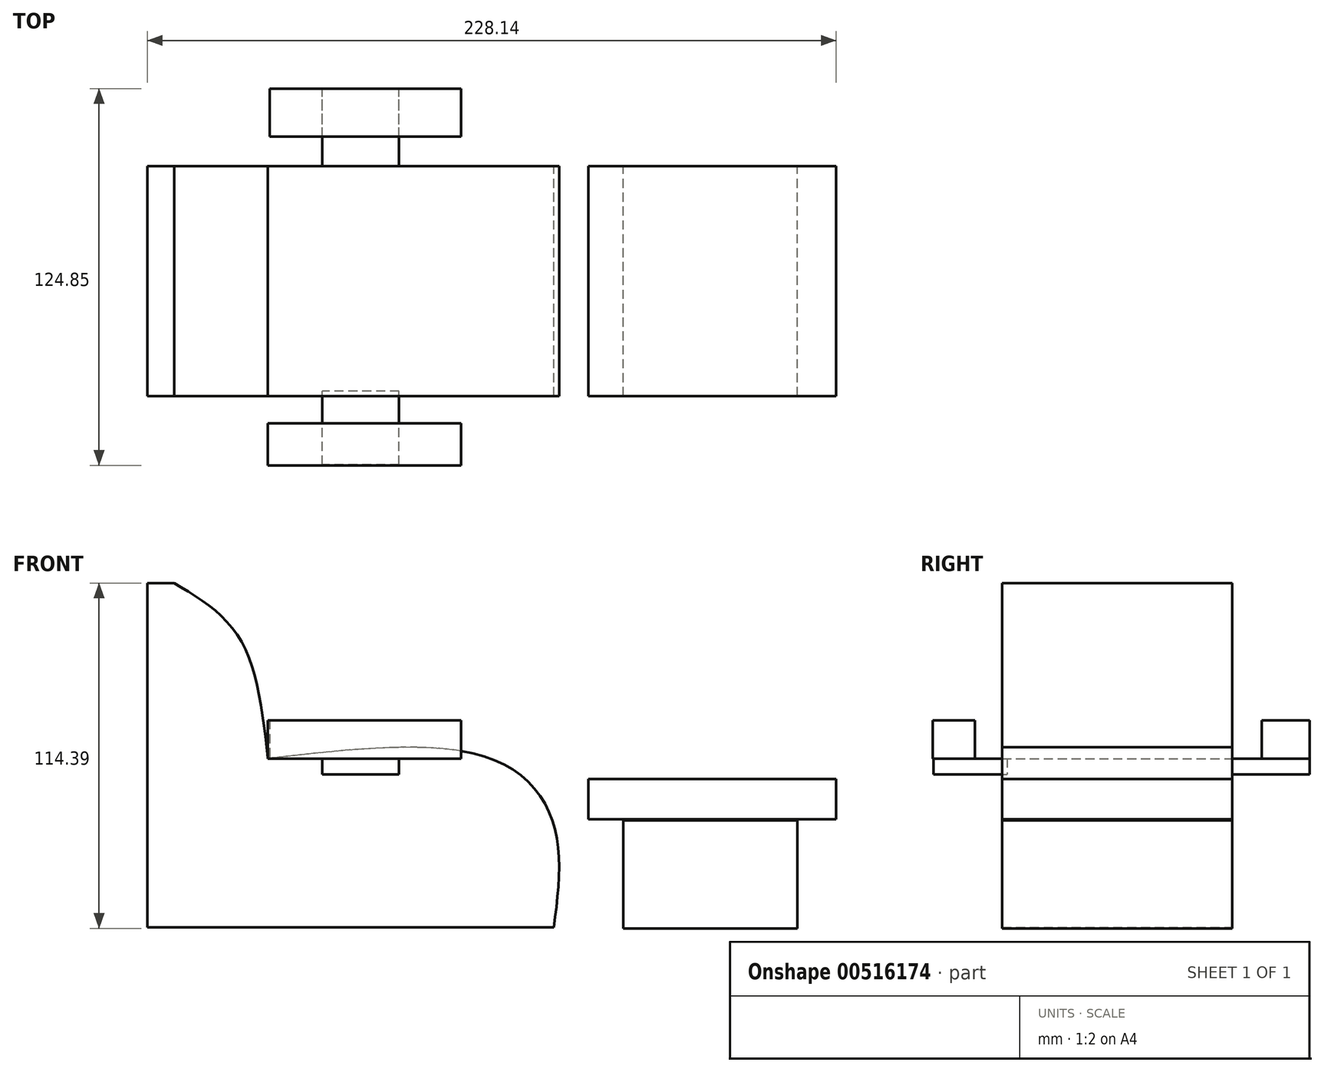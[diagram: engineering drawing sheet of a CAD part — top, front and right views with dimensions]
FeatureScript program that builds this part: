
annotation { "Feature Type Name" : "Feature", "Feature Type Description" : "" }
export const myFeature = defineFeature(function(context is Context, id is Id, definition is map)
    precondition{}
    {
        {
            var Q0;
            Q0=qCreatedBy(makeId("Front.planeOp"),FACE);
            var sketch = newSketch(context, id + "F0", { "sketchPlane" : qUnion([Q0])});
            skFitSpline(sketch, "E0", {"points": [v(-49.12, 58.15) * mm, v(-27.57, 40.08) * mm, v(-18.06, 0) * mm], "startDerivative": vector(54.48, -32.4) * mm, "endDerivative": vector(9.07, -82.3) * mm});
            skLineSegment(sketch, "E1", {"start": v(-49.12, 58.15) * mm, "end": v(-57.99, 58.15) * mm});
            skLineSegment(sketch, "E2", {"start": v(-57.99, 58.15) * mm, "end": v(-57.99, 0) * mm});
            skLineSegment(sketch, "E3", {"start": v(-57.99, 0) * mm, "end": v(-57.99, -55.93) * mm});
            skLineSegment(sketch, "E4", {"start": v(-57.99, -55.93) * mm, "end": v(76.68, -55.93) * mm});
            skFitSpline(sketch, "E5", {"points": [v(76.68, -55.93) * mm, v(76.68, -22.02) * mm, v(55.77, 0) * mm, v(-18.06, 0) * mm], "startDerivative": vector(15.36, 121.65) * mm, "endDerivative": vector(-195.91, -22.64) * mm});
            skSolve(sketch);
        }
        {
            var Q0;
            Q0 = qSketchRegion(id + "F0", true);
            extrude(context, id + "F1", {"entities" : qUnion([Q0]), "depth" : 76.2 * mm, "offsetDistance" : 25.4 * mm});
        }
        {
            var Q0;
            Q0=qCreatedBy(makeId("Top.planeOp"),FACE);
            var sketch = newSketch(context, id + "F2", { "sketchPlane" : qUnion([Q0])});
            skLineSegment(sketch, "E6.bottom", {"start": v(-18.09, -99.18) * mm, "end": v(45.92, -99.18) * mm});
            skLineSegment(sketch, "E6.top", {"start": v(-18.09, -85.24) * mm, "end": v(45.92, -85.24) * mm});
            skLineSegment(sketch, "E6.left", {"start": v(-18.09, -99.18) * mm, "end": v(-18.09, -85.24) * mm});
            skLineSegment(sketch, "E6.right", {"start": v(45.92, -99.18) * mm, "end": v(45.92, -85.24) * mm});
            skLineSegment(sketch, "E7.bottom", {"start": v(-17.45, 9.82) * mm, "end": v(45.92, 9.82) * mm});
            skLineSegment(sketch, "E7.top", {"start": v(-17.45, 25.67) * mm, "end": v(45.92, 25.67) * mm});
            skLineSegment(sketch, "E7.left", {"start": v(-17.45, 9.82) * mm, "end": v(-17.45, 25.67) * mm});
            skLineSegment(sketch, "E7.right", {"start": v(45.92, 9.82) * mm, "end": v(45.92, 25.67) * mm});
            skSolve(sketch);
        }
        {
            var Q0;
            Q0 = qSketchRegion(id + "F2", true);
            extrude(context, id + "F3", {"entities" : qUnion([Q0]), "depth" : 12.7 * mm, "offsetDistance" : 25.4 * mm});
        }
        {
            var Q0;
            Q0=qCreatedBy(makeId("Right.planeOp"),FACE);
            var sketch = newSketch(context, id + "F4", { "sketchPlane" : qUnion([Q0])});
            skLineSegment(sketch, "E8.bottom", {"start": v(0, 0) * mm, "end": v(25.58, 0) * mm});
            skLineSegment(sketch, "E8.top", {"start": v(0, -5.23) * mm, "end": v(25.58, -5.23) * mm});
            skLineSegment(sketch, "E8.left", {"start": v(0, 0) * mm, "end": v(0, -5.23) * mm});
            skLineSegment(sketch, "E8.right", {"start": v(25.58, 0) * mm, "end": v(25.58, -5.23) * mm});
            skLineSegment(sketch, "E9.bottom", {"start": v(-98.95, 0) * mm, "end": v(-74.55, 0) * mm});
            skLineSegment(sketch, "E9.top", {"start": v(-98.95, -5.23) * mm, "end": v(-74.55, -5.23) * mm});
            skLineSegment(sketch, "E9.left", {"start": v(-98.95, 0) * mm, "end": v(-98.95, -5.23) * mm});
            skLineSegment(sketch, "E9.right", {"start": v(-74.55, 0) * mm, "end": v(-74.55, -5.23) * mm});
            skSolve(sketch);
        }
        {
            var Q0;
            Q0 = qSketchRegion(id + "F4", true);
            extrude(context, id + "F5", {"entities" : qUnion([Q0]), "depth" : 25.4 * mm, "offsetDistance" : 25.4 * mm});
        }
        {
            var Q0;
            Q0=qCreatedBy(makeId("Front.planeOp"),FACE);
            var sketch = newSketch(context, id + "F6", { "sketchPlane" : qUnion([Q0])});
            skLineSegment(sketch, "E10.bottom", {"start": v(99.63, -20.44) * mm, "end": v(157.3, -20.44) * mm});
            skLineSegment(sketch, "E10.top", {"start": v(99.63, -56.24) * mm, "end": v(157.3, -56.24) * mm});
            skLineSegment(sketch, "E10.left", {"start": v(99.63, -20.44) * mm, "end": v(99.63, -56.24) * mm});
            skLineSegment(sketch, "E10.right", {"start": v(157.3, -20.44) * mm, "end": v(157.3, -56.24) * mm});
            skSolve(sketch);
        }
        {
            var Q0;
            Q0 = qSketchRegion(id + "F6", true);
            extrude(context, id + "F7", {"entities" : qUnion([Q0]), "depth" : 76.2 * mm, "offsetDistance" : 25.4 * mm});
        }
        {
            var Q0;
            Q0=qCreatedBy(makeId("Front.planeOp"),FACE);
            var sketch = newSketch(context, id + "F8", { "sketchPlane" : qUnion([Q0])});
            skLineSegment(sketch, "E11.bottom", {"start": v(88.08, -20.12) * mm, "end": v(170.15, -20.12) * mm});
            skLineSegment(sketch, "E11.top", {"start": v(88.08, -6.81) * mm, "end": v(170.15, -6.81) * mm});
            skLineSegment(sketch, "E11.left", {"start": v(88.08, -20.12) * mm, "end": v(88.08, -6.81) * mm});
            skLineSegment(sketch, "E11.right", {"start": v(170.15, -20.12) * mm, "end": v(170.15, -6.81) * mm});
            skSolve(sketch);
        }
        {
            var Q0;
            Q0 = qSketchRegion(id + "F8", true);
            extrude(context, id + "F9", {"entities" : qUnion([Q0]), "depth" : 76.2 * mm, "offsetDistance" : 25.4 * mm});
        }
    });
